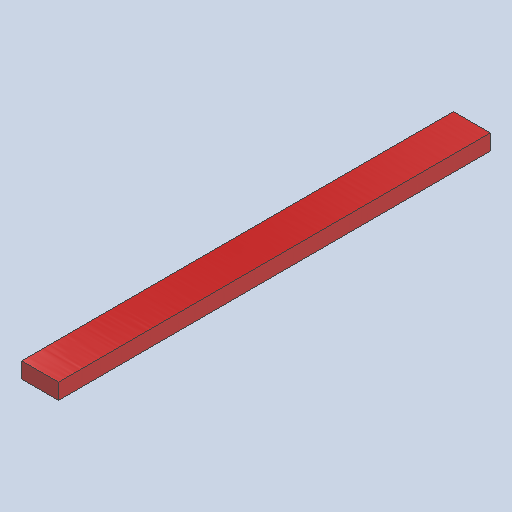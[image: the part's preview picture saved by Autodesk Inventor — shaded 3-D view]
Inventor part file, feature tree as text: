
AUTODESK INVENTOR PART (.ipt)
format: ipt  version: 2025.1 (Build 291241020, 241B)  size: 92,672 bytes
history: native  units: in
note: dims shown in document units (in); Inventor stores cm internally (conversion verified against a paired STEP export)
features: other x3, plane x1, extrude x1, sketch x1
ambient origin geometry x8: Origin, YZ Plane, XZ Plane, XY Plane, X Axis, Y Axis, Z Axis, Center Point
bodies: Solid1 (feature_tree)
feature tree (6):
  plane  "Work Plane1"
  extrude  "Extrusion1"  Depth=3.5in
  sketch  "Sketch1"  dims[d0=1.5in d1=3.5in d2=41.0in d3=0.0in]
  other  "Finish1"
  other  "Assembly2"
  other  "8'x2x4:1"
